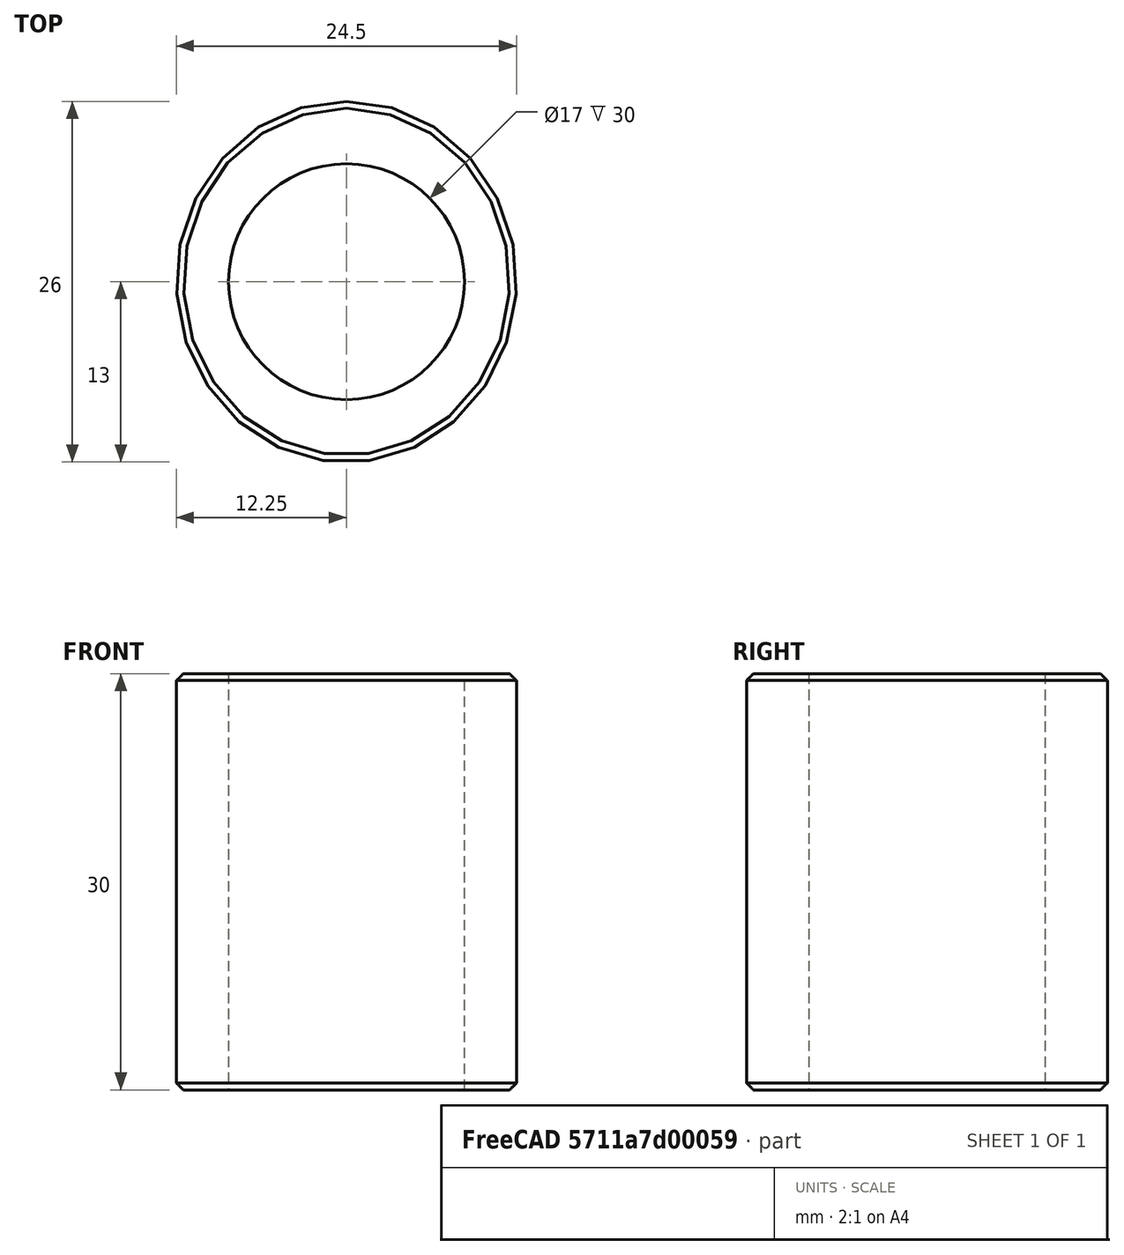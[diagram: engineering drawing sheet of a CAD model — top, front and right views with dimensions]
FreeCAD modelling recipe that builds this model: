
FCSTD DOCUMENT  (FreeCAD 1.1R44227 +568 (Git))
Label: frame_side
License: All rights reserved
LicenseURL: https://en.wikipedia.org/wiki/All_rights_reserved
objects: App::Point×1, Sketcher::SketchObject×1, PartDesign::Pad×1, PartDesign::Chamfer×1, PartDesign::Body×1
note: 9 computed .brp shape members not serialized (recipe doc carries the construction recipe); baked Part::Feature solids carry a one-line shape summary decoded from their .brp

FEATURE [App::Point] Origin001
  Role = Origin
FEATURE [Sketcher::SketchObject] Sketch
  ArcFitTolerance = 1e-06
  AttachmentSupport = -> [Origin]
  ExternalTypes = [0]
  FullyConstrained = true
  MakeInternals = false
  MapMode = 5
  _ExternalGeoVersion = 1
  sketch-geometry (6):
    g0: Ellipse CenterX=0 CenterY=0 CenterZ=0 NormalX=0 NormalY=0 NormalZ=1 MajorRadius=13 MinorRadius=12.25 AngleXU=1.5708
    g1: LineSegment [constr] StartX=0 StartY=13 StartZ=0 EndX=0 EndY=-13 EndZ=0
    g2: LineSegment [constr] StartX=-12.25 StartY=1e-16 StartZ=0 EndX=12.25 EndY=-1e-16 EndZ=0
    g3: GeomPoint [constr] X=-2e-16 Y=4.35172 Z=0
    g4: GeomPoint [constr] X=2e-16 Y=-4.35172 Z=0
    g5: Circle CenterX=0 CenterY=0 CenterZ=0 NormalX=0 NormalY=0 NormalZ=1 AngleXU=0 Radius=8.5
  constraints (7):
    c: InternalAlignment(g1-g4 -> g0) x4
    c: Coincident(g0,g-1)
    c: DistanceY(g1,g1) = 26
    c: DistanceX(g2,g2) = 24.5
    c: Vertical(g1)
    c: Coincident(g5,g0)
    c: Diameter(g5) = 17
FEATURE [PartDesign::Pad] Pad
  Direction = (0,0,1)
  Length = 30
  Length2 = 10
  Profile = -> Sketch
  ReferenceAxis = -> Sketch [N_Axis]
  Refine = true
  SideType = 0
  Suppressed = false
  Type = 0
  Type2 = 0
FEATURE [PartDesign::Chamfer] Chamfer
  Angle = 45
  Base = -> Pad [Edge3,Edge2]
  BaseFeature = -> Pad
  ChamferType = 0
  FlipDirection = false
  Refine = true
  Size = 0.5
  Size2 = 1
  SupportTransform = false
  Suppressed = false
  UseAllEdges = false
FEATURE [PartDesign::Body] Body
  AllowCompound = true
  Group = -> [Sketch,Pad,Chamfer]
  Origin = -> Origin
  Tip = -> Chamfer
